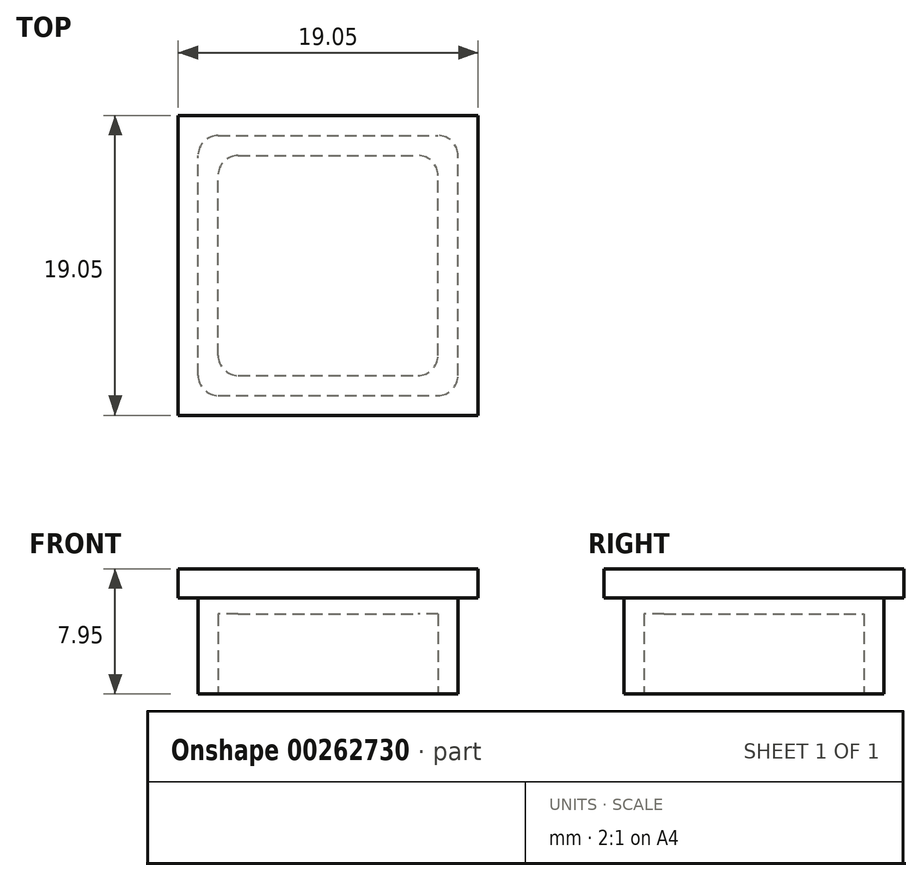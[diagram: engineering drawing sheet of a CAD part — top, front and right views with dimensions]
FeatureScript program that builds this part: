
annotation { "Feature Type Name" : "Feature", "Feature Type Description" : "" }
export const myFeature = defineFeature(function(context is Context, id is Id, definition is map)
    precondition{}
    {
        {
            var Q0;
            Q0=qCreatedBy(makeId("Top.planeOp"),FACE);
            var sketch = newSketch(context, id + "F0", { "sketchPlane" : qUnion([Q0])});
            skLineSegment(sketch, "E0.bottom", {"start": v(1.27, 0) * mm, "end": v(15.24, 0) * mm});
            skLineSegment(sketch, "E0.top", {"start": v(1.27, 16.51) * mm, "end": v(15.24, 16.51) * mm});
            skLineSegment(sketch, "E0.left", {"start": v(0, 1.27) * mm, "end": v(0, 15.24) * mm});
            skLineSegment(sketch, "E0.right", {"start": v(16.51, 1.27) * mm, "end": v(16.51, 15.24) * mm});
            skPoint(sketch, "E1.visualSharp", {"position": v(0, 16.51) * mm});
            skArc(sketch, "E1.filletArc", {"start": v(1.27, 16.51) * mm, "mid": v(0.37, 16.14) * mm, "end": v(0, 15.24) * mm});
            skPoint(sketch, "E2.visualSharp", {"position": v(16.51, 16.51) * mm});
            skArc(sketch, "E2.filletArc", {"start": v(16.51, 15.24) * mm, "mid": v(16.14, 16.14) * mm, "end": v(15.24, 16.51) * mm});
            skPoint(sketch, "E3.visualSharp", {"position": v(16.51, 0) * mm});
            skArc(sketch, "E3.filletArc", {"start": v(15.24, 0) * mm, "mid": v(16.14, 0.37) * mm, "end": v(16.51, 1.27) * mm});
            skPoint(sketch, "E4.visualSharp", {"position": v(0, 0) * mm});
            skArc(sketch, "E4.filletArc", {"start": v(0, 1.27) * mm, "mid": v(0.37, 0.37) * mm, "end": v(1.27, 0) * mm});
            skPoint(sketch, "E5", {"position": v(8.26, 8.26) * mm});
            skPoint(sketch, "E5.positionSnap0", {"position": v(16.51, 8.26) * mm});
            skPoint(sketch, "E5.positionSnap1", {"position": v(8.26, 0) * mm});
            skSolve(sketch);
        }
        {
            var Q0;
            Q0 = qSketchRegion(id + "F0", true);
            extrude(context, id + "F1", {"entities" : qUnion([Q0]), "oppositeDirection" : true, "depth" : 6.1 * mm});
        }
        {
            var Q0;
            Q0=makeQuery(id+"F1.opExtrude","CAP_FACE",FACE,{"disambiguationData":[OSD([sQuery(id+"F0.wireOp",EDGE,"E0.bottom"),sQuery(id+"F0.wireOp",EDGE,"E0.top"),sQuery(id+"F0.wireOp",EDGE,"E0.left"),sQuery(id+"F0.wireOp",EDGE,"E0.right"),sQuery(id+"F0.wireOp",EDGE,"E1.filletArc"),sQuery(id+"F0.wireOp",EDGE,"E2.filletArc"),sQuery(id+"F0.wireOp",EDGE,"E3.filletArc"),sQuery(id+"F0.wireOp",EDGE,"E4.filletArc")])],"isStart":false});
            var sketch = newSketch(context, id + "F2", { "sketchPlane" : qUnion([Q0])});
            skLineSegment(sketch, "E6.bottom", {"start": v(2.54, -1.27) * mm, "end": v(13.97, -1.27) * mm});
            skLineSegment(sketch, "E6.top", {"start": v(2.54, -15.24) * mm, "end": v(13.97, -15.24) * mm});
            skLineSegment(sketch, "E6.left", {"start": v(1.27, -2.54) * mm, "end": v(1.27, -13.97) * mm});
            skLineSegment(sketch, "E6.right", {"start": v(15.24, -2.54) * mm, "end": v(15.24, -13.97) * mm});
            skPoint(sketch, "E7.visualSharp", {"position": v(1.27, -1.27) * mm});
            skArc(sketch, "E7.filletArc", {"start": v(2.54, -1.27) * mm, "mid": v(1.64, -1.64) * mm, "end": v(1.27, -2.54) * mm});
            skPoint(sketch, "E8.visualSharp", {"position": v(15.24, -1.27) * mm});
            skArc(sketch, "E8.filletArc", {"start": v(15.24, -2.54) * mm, "mid": v(14.87, -1.64) * mm, "end": v(13.97, -1.27) * mm});
            skPoint(sketch, "E9.visualSharp", {"position": v(15.24, -15.24) * mm});
            skArc(sketch, "E9.filletArc", {"start": v(13.97, -15.24) * mm, "mid": v(14.87, -14.87) * mm, "end": v(15.24, -13.97) * mm});
            skPoint(sketch, "E10.visualSharp", {"position": v(1.27, -15.24) * mm});
            skArc(sketch, "E10.filletArc", {"start": v(1.27, -13.97) * mm, "mid": v(1.64, -14.87) * mm, "end": v(2.54, -15.24) * mm});
            skSolve(sketch);
        }
        {
            var Q0;
            Q0 = qSketchRegion(id + "F2", true);
            extrude(context, id + "F3", {"entities" : qUnion([Q0]), "operationType" : NewBodyOperationType.REMOVE, "oppositeDirection" : true, "depth" : 5.08 * mm});
        }
        {
            var Q0;
            Q0=qCreatedBy(makeId("Top.planeOp"),FACE);
            var sketch = newSketch(context, id + "F4", { "sketchPlane" : qUnion([Q0])});
            skLineSegment(sketch, "E11.bottom", {"start": v(-1.27, 17.78) * mm, "end": v(17.78, 17.78) * mm});
            skLineSegment(sketch, "E11.top", {"start": v(-1.27, -1.27) * mm, "end": v(17.78, -1.27) * mm});
            skLineSegment(sketch, "E11.left", {"start": v(-1.27, 17.78) * mm, "end": v(-1.27, -1.27) * mm});
            skLineSegment(sketch, "E11.right", {"start": v(17.78, 17.78) * mm, "end": v(17.78, -1.27) * mm});
            skSolve(sketch);
        }
        {
            var Q0;
            Q0 = qSketchRegion(id + "F4", true);
            extrude(context, id + "F5", {"entities" : qUnion([Q0]), "operationType" : NewBodyOperationType.ADD, "depth" : 1.85 * mm});
        }
    });
